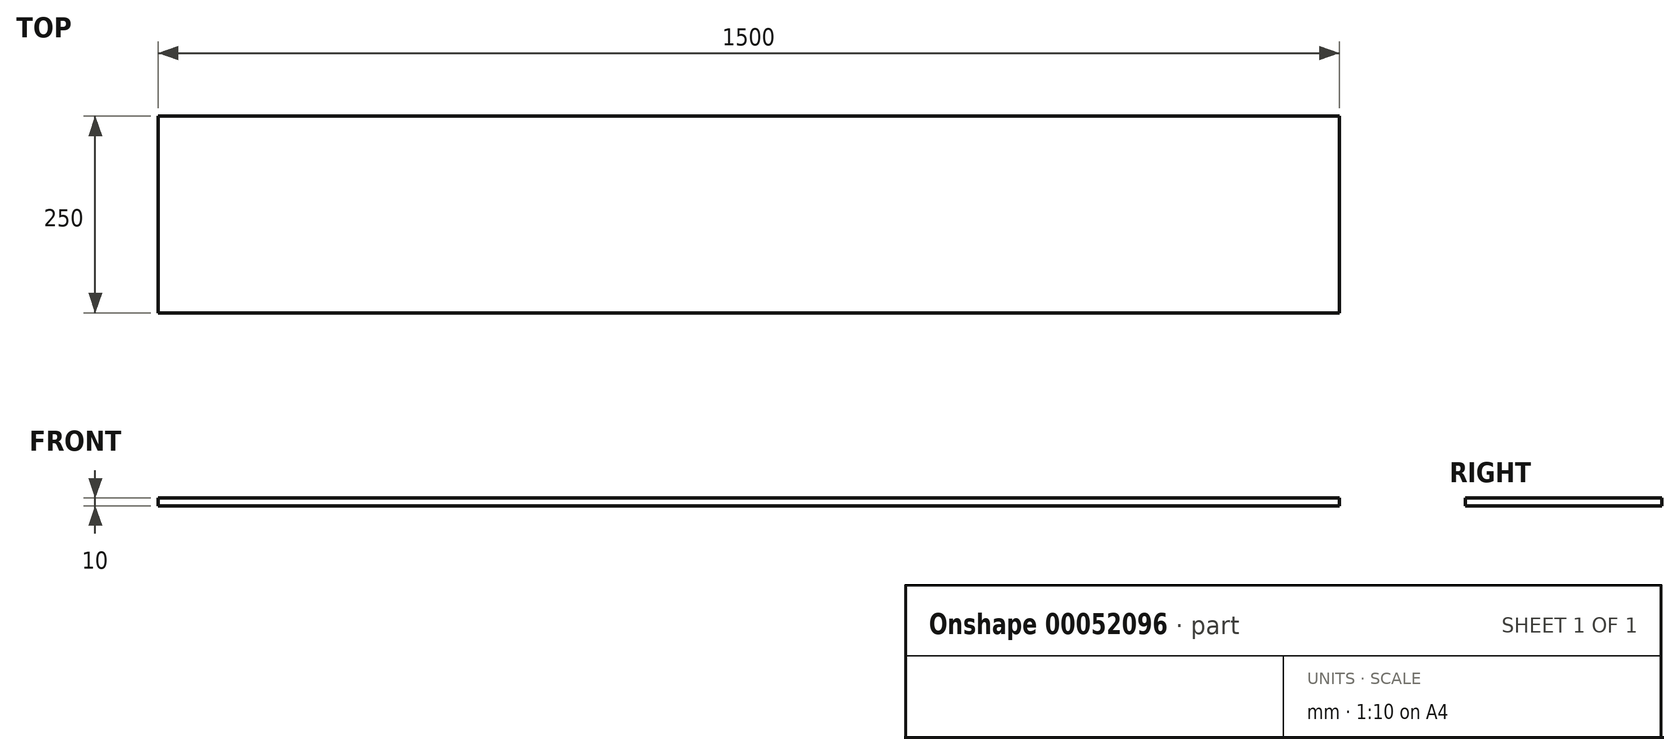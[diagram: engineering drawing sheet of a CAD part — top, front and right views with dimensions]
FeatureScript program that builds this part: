
annotation { "Feature Type Name" : "Feature", "Feature Type Description" : "" }
export const myFeature = defineFeature(function(context is Context, id is Id, definition is map)
    precondition{}
    {
        {
            var Q0;
            Q0=qCreatedBy(makeId("Top.planeOp"),FACE);
            var sketch = newSketch(context, id + "F0", { "sketchPlane" : qUnion([Q0])});
            skLineSegment(sketch, "E0.bottom", {"start": v(0, 0) * mm, "end": v(1500, 0) * mm});
            skLineSegment(sketch, "E0.top", {"start": v(0, 250) * mm, "end": v(1500, 250) * mm});
            skLineSegment(sketch, "E0.left", {"start": v(0, 0) * mm, "end": v(0, 250) * mm});
            skLineSegment(sketch, "E0.right", {"start": v(1500, 0) * mm, "end": v(1500, 250) * mm});
            skSolve(sketch);
        }
        {
            var Q0;
            Q0=makeQuery(id+"F0.imprint","IMPRINT",FACE,{"disambiguationData":[TD([[makeQuery(id+"F0.imprint","IMPRINT",EDGE,{"derivedFrom":sQuery(id+"F0.wireOp",EDGE,"E0.bottom")}),1.0]])]});
            extrude(context, id + "F1", {"entities" : qUnion([Q0]), "depth" : 10 * mm});
        }
    });
